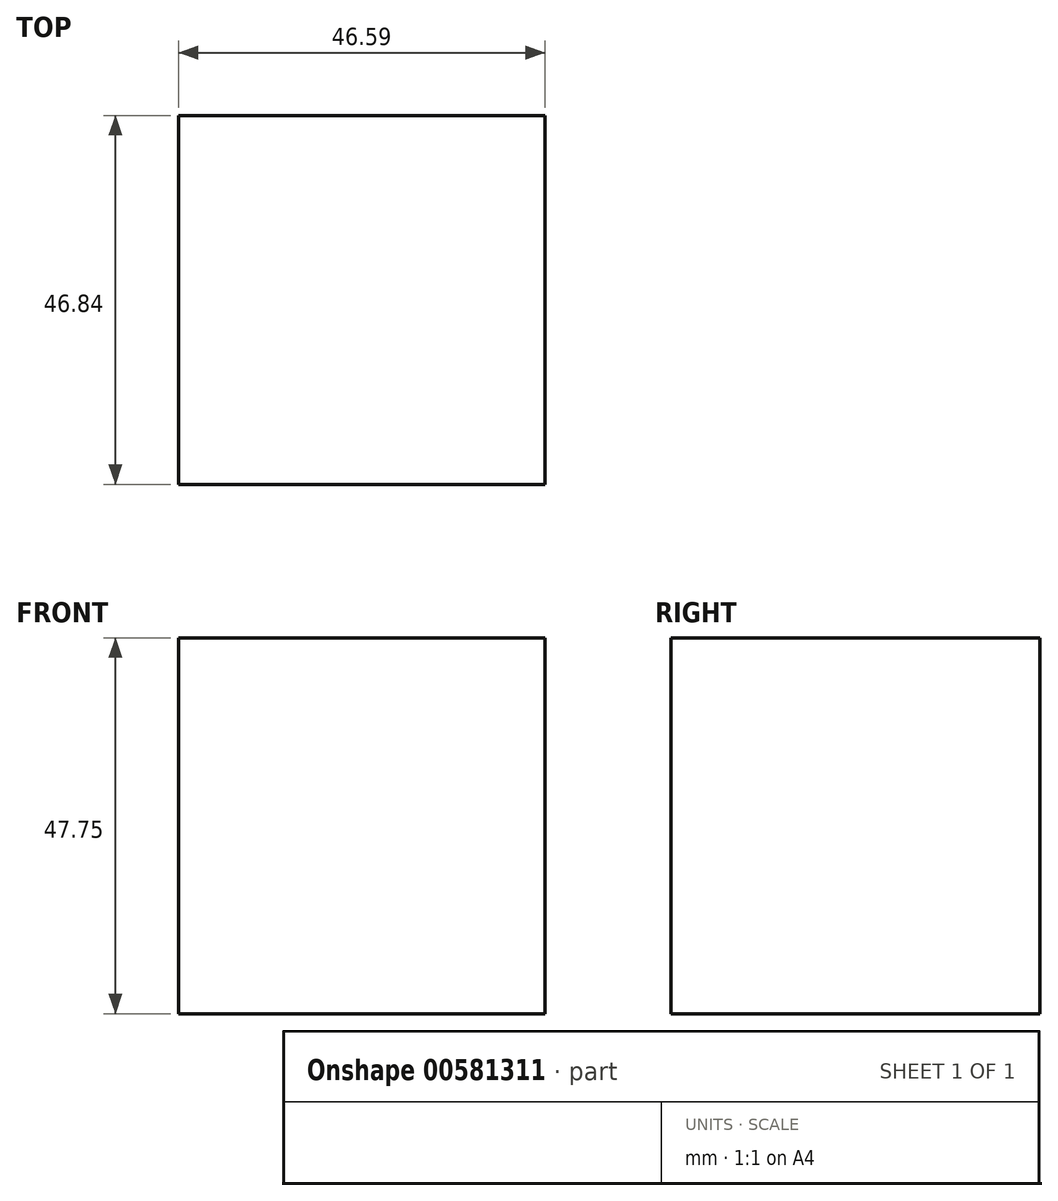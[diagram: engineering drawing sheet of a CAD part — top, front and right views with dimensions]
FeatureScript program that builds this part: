
annotation { "Feature Type Name" : "Feature", "Feature Type Description" : "" }
export const myFeature = defineFeature(function(context is Context, id is Id, definition is map)
    precondition{}
    {
        {
            var Q0;
            Q0=qCreatedBy(makeId("Top.planeOp"),FACE);
            var sketch = newSketch(context, id + "F0", { "sketchPlane" : qUnion([Q0])});
            skLineSegment(sketch, "E0.bottom", {"start": v(0, 0) * mm, "end": v(46.59, 0) * mm});
            skLineSegment(sketch, "E0.top", {"start": v(0, 46.84) * mm, "end": v(46.59, 46.84) * mm});
            skLineSegment(sketch, "E0.left", {"start": v(0, 0) * mm, "end": v(0, 46.84) * mm});
            skLineSegment(sketch, "E0.right", {"start": v(46.59, 0) * mm, "end": v(46.59, 46.84) * mm});
            skSolve(sketch);
        }
        {
            var Q0;
            Q0 = qSketchRegion(id + "F0", true);
            extrude(context, id + "F1", {"entities" : qUnion([Q0]), "depth" : 47.75 * mm, "offsetDistance" : 25.4 * mm});
        }
    });
